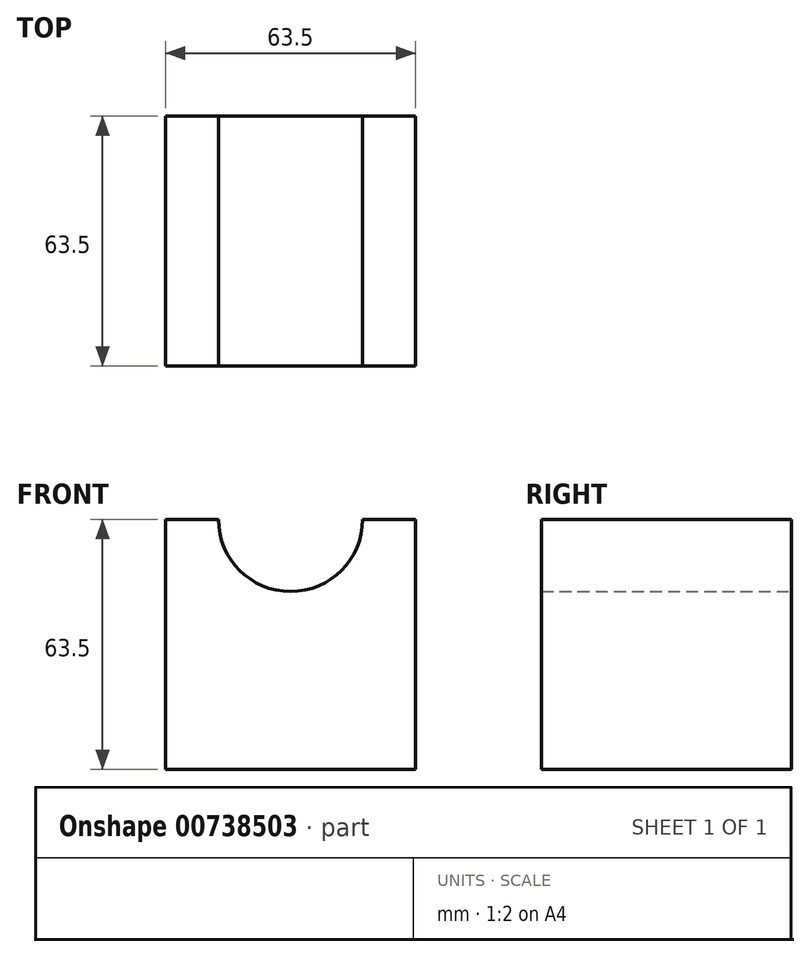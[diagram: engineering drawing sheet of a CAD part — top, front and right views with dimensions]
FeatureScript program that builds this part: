
annotation { "Feature Type Name" : "Feature", "Feature Type Description" : "" }
export const myFeature = defineFeature(function(context is Context, id is Id, definition is map)
    precondition{}
    {
        {
            var Q0;
            Q0=qCreatedBy(makeId("Front.planeOp"),FACE);
            var sketch = newSketch(context, id + "F0", { "sketchPlane" : qUnion([Q0])});
            skLineSegment(sketch, "E0.bottom", {"start": v(-33.25, 40.92) * mm, "end": v(30.25, 40.92) * mm});
            skLineSegment(sketch, "E0.top", {"start": v(-33.25, -22.58) * mm, "end": v(30.25, -22.58) * mm});
            skLineSegment(sketch, "E0.left", {"start": v(-33.25, 40.92) * mm, "end": v(-33.25, -22.58) * mm});
            skLineSegment(sketch, "E0.right", {"start": v(30.25, 40.92) * mm, "end": v(30.25, -22.58) * mm});
            skArc(sketch, "E1", {"start": v(-19.79, 40.92) * mm, "mid": v(-1.5, 22.63) * mm, "end": v(16.79, 40.92) * mm});
            skSolve(sketch);
        }
        {
            var Q0;
            Q0=makeQuery(id+"F0.imprint","IMPRINT",FACE,{"disambiguationData":[TD([[makeQuery(id+"F0.imprint","IMPRINT",EDGE,{"derivedFrom":sQuery(id+"F0.wireOp",EDGE,"E0.top")}),1.0]])]});
            extrude(context, id + "F1", {"entities" : qUnion([Q0]), "depth" : 63.5 * mm, "offsetDistance" : 25.4 * mm});
        }
    });
